# Revit family: Faucet_Touchless-Wall_Mount-Lavatory-KOHLER-Composed-K-EX25998T
name_source: partatom
category: Plumbing Fixtures
units: mm (PartAtom-declared; Revit-internal decimal feet)

## family parameters
Cut with Voids When Loaded = No
Host = Face
OmniClass Number = 23.31.11.00
OmniClass Title = Faucets
Part Type = Normal
Room Calculation Point = No
Round Connector Dimension = Use Diameter
Shared = No

## types (4) — shared parameters
ADA Compliant = No
Apparent Load = 0 VA
Assembly Code = D2010
CW Connection = Yes
Cold Water Inlet = Cold Water Inlet
Date Modified = 12/13/2022
Default Elevation = 36"
Drain Included = Yes
Electrical Connector = Yes
Electrical Note = One Dedicated Circuit Required
Faucet Hole Spacing = 0"
HW Connection = No
Handle Clearance = 0"
Height = 2 3/8"
Hot Water Inlet = Hot Water Inlet
Length = 8 7/16"
Manufacturer = Kohler Co.
Master Format 2014 = 22 41 39
Master Format 2014 Name = Residential Faucets, Supplies, and Trim
Material = Premium Metal Construction
Pressure = 0.00 psi
Product Documentation Link = https://files.kohler.com.cn
Product Name = Composed
Product Page URL = https://www.kohler.com.cn
Spout Reach = 8 7/16"
URL = http://www.kohler.com.cn
Vent Connection = No
Voltage = 220 V
Waste Connection = No
Waste Water Outlet = Waste Water Outlet
WaterSense Certified = No
Width = 2 3/8"

## per-type parameters (varying)
| type | Description | Finish | Flow Rate | Model | Secondary Finish | Type |
| 0.5 GPM, CP-Polished Chrome | Boshi In-Wall Sensor Faucet Single Cooling, 1.9 Liters, Without Power Box | Kohler-Metal-CP-Polished_Chrome | 1 GPM | K-EX25998T-NW-CP | Kohler-Plastic-58-Thunder_Grey | 1 |
| 0.5 GPM, BN-Vibrant Brushed Nickel | Boshi In-Wall Sensor Faucet Single Cooling, 1.9 Liters, Without Power Box | Kohler-Metal-BN-Vibrant_Brushed_Nickel | 1 GPM | K-EX25998T-NW-BN | Kohler-Plastic-58-Thunder_Grey | 2 |
| 0.35 GPM, CP-Polished Chrome | Busch In-Wall Sensor Faucet Single Cool, 1.4 Liters, Without Power Box | Kohler-Metal-CP-Polished_Chrome | 0 GPM | K-EX25998T-NWS3-CP | Kohler-Plastic-95-Ice_Grey | 3 |
| 0.26 GPM, CP-Polished Chrome | Bashi In-Wall Sensor Faucet Single Cooling, 1.0 Litres, Without Power Box | Kohler-Metal-CP-Polished_Chrome | 0 GPM | K-EX25998T-NWS5-CP | Kohler-Plastic-95-Ice_Grey | 4 |

## geometry (parser evidence)
native form markers: Sweep x7
no freeform markers — native parametric forms only
